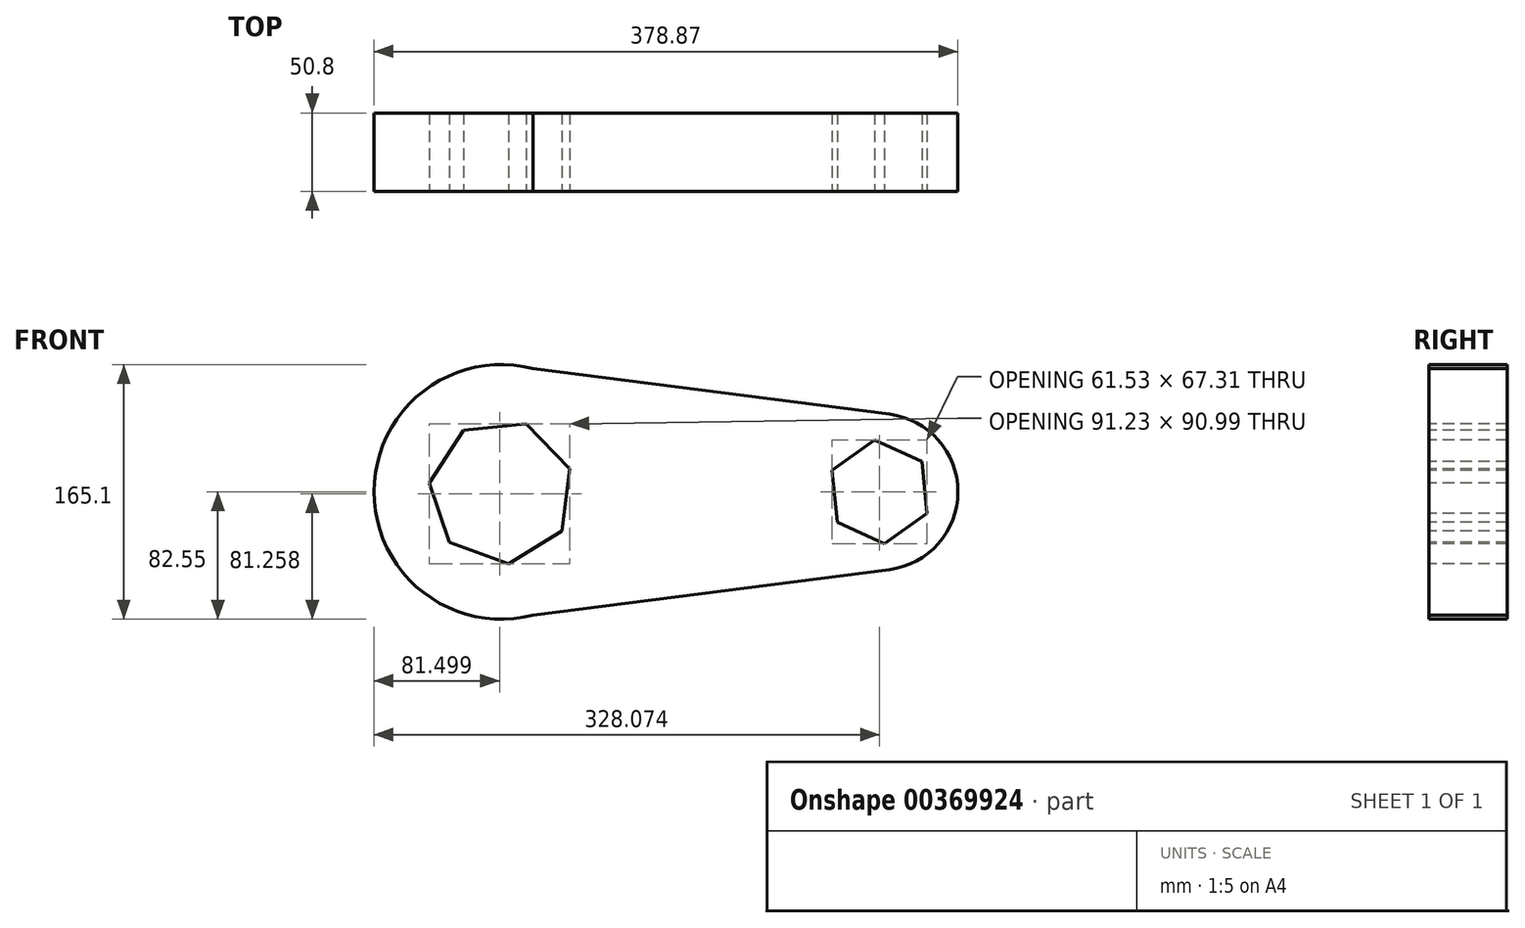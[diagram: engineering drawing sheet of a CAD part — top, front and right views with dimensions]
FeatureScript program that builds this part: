
annotation { "Feature Type Name" : "Feature", "Feature Type Description" : "" }
export const myFeature = defineFeature(function(context is Context, id is Id, definition is map)
    precondition{}
    {
        {
            var Q0;
            Q0=qCreatedBy(makeId("Front.planeOp"),FACE);
            var sketch = newSketch(context, id + "F0", { "sketchPlane" : qUnion([Q0])});
            skCircle(sketch, "E0", {"center": v(0, 0) * mm, "radius": 82.55 * mm});
            skCircle(sketch, "E1", {"center": v(245.52, 0) * mm, "radius": 50.8 * mm});
            skLineSegment(sketch, "E2", {"start": v(0, 82.55) * mm, "end": v(251.96, 50.4) * mm});
            skLineSegment(sketch, "E3", {"start": v(0, -82.55) * mm, "end": v(251.96, -50.4) * mm});
            skCircle(sketch, "E4.cCircle", {"center": v(0, 0) * mm, "radius": 42.37 * mm, "construction": true});
            skLineSegment(sketch, "E4.0", {"start": v(39.52, -25.48) * mm, "end": v(4.72, -46.79) * mm});
            skLineSegment(sketch, "E4.1", {"start": v(4.72, -46.79) * mm, "end": v(-33.64, -32.86) * mm});
            skLineSegment(sketch, "E4.2", {"start": v(-33.64, -32.86) * mm, "end": v(-46.66, 5.8) * mm});
            skLineSegment(sketch, "E4.3", {"start": v(-46.66, 5.8) * mm, "end": v(-24.55, 40.1) * mm});
            skLineSegment(sketch, "E4.4", {"start": v(-24.55, 40.1) * mm, "end": v(16.05, 44.2) * mm});
            skLineSegment(sketch, "E4.5", {"start": v(16.05, 44.2) * mm, "end": v(44.56, 15.01) * mm});
            skLineSegment(sketch, "E4.6", {"start": v(44.56, 15.01) * mm, "end": v(39.52, -25.48) * mm});
            skPoint(sketch, "E4.0.midPoint", {"position": v(22.12, -36.13) * mm});
            skCircle(sketch, "E5.cCircle", {"center": v(245.52, 0) * mm, "radius": 29.28 * mm, "construction": true});
            skLineSegment(sketch, "E5.0", {"start": v(276.29, -14.03) * mm, "end": v(248.76, -33.66) * mm});
            skLineSegment(sketch, "E5.1", {"start": v(248.76, -33.66) * mm, "end": v(218, -19.63) * mm});
            skLineSegment(sketch, "E5.2", {"start": v(218, -19.63) * mm, "end": v(214.76, 14.03) * mm});
            skLineSegment(sketch, "E5.3", {"start": v(214.76, 14.03) * mm, "end": v(242.3, 33.66) * mm});
            skLineSegment(sketch, "E5.4", {"start": v(242.3, 33.66) * mm, "end": v(273.06, 19.63) * mm});
            skLineSegment(sketch, "E5.5", {"start": v(273.06, 19.63) * mm, "end": v(276.29, -14.03) * mm});
            skPoint(sketch, "E5.0.midPoint", {"position": v(262.52, -23.84) * mm});
            skSolve(sketch);
        }
        {
            var Q0;
            Q0 = qSketchRegion(id + "FuOrrWb41KMFV91_0", true);
            var Q1;
            Q1 = qSketchRegion(id + "F0", true);
            extrude(context, id + "F1", {"entities" : qUnion([Q0, Q1]), "oppositeDirection" : true, "depth" : 50.8 * mm});
        }
    });
